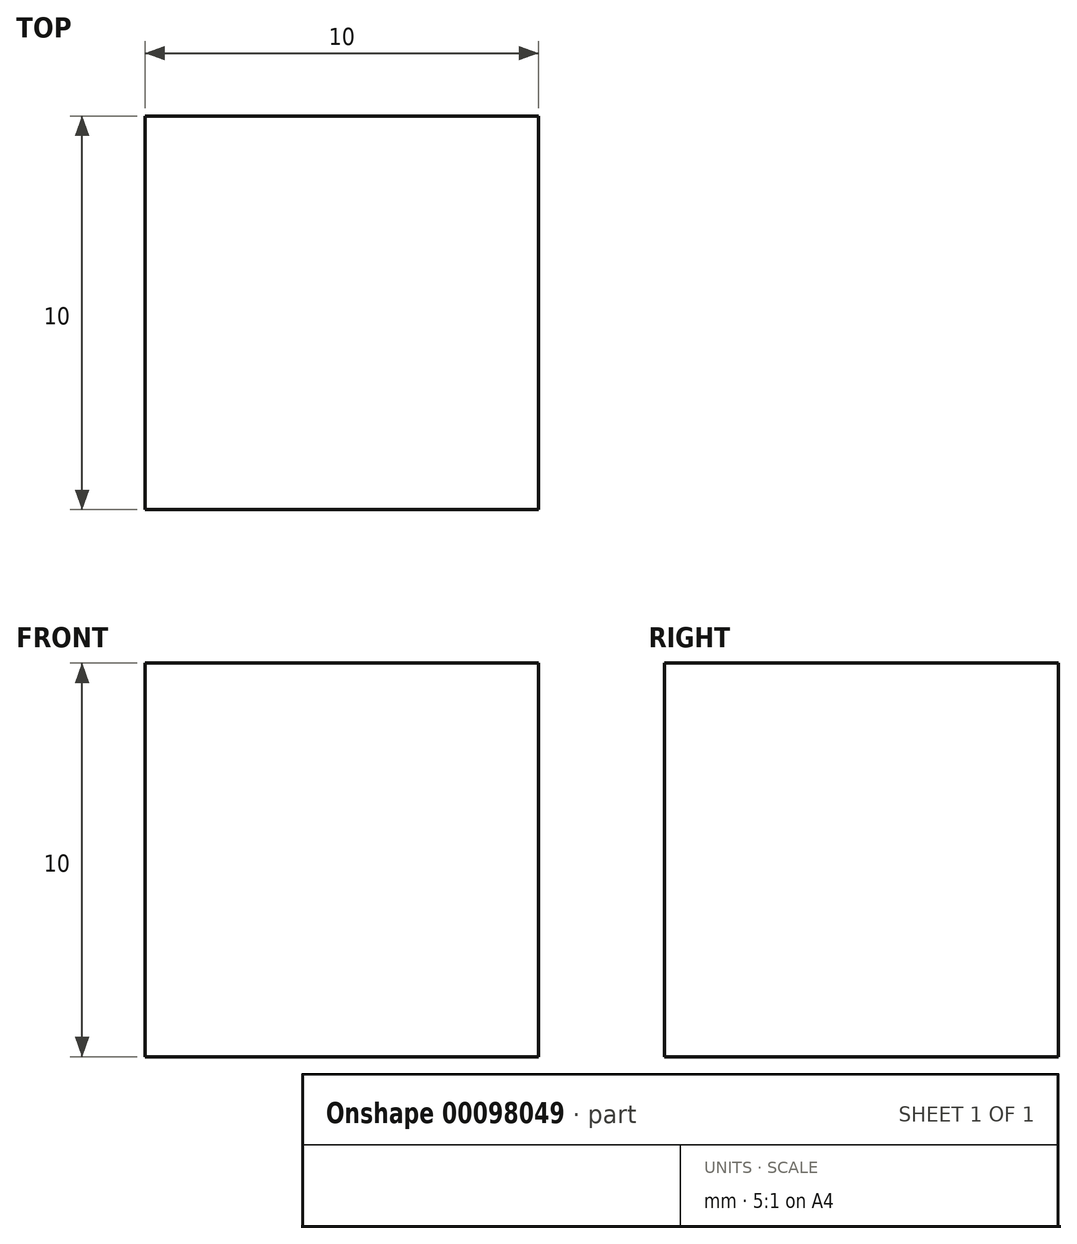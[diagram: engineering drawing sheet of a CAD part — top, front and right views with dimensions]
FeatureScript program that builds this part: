
annotation { "Feature Type Name" : "Feature", "Feature Type Description" : "" }
export const myFeature = defineFeature(function(context is Context, id is Id, definition is map)
    precondition{}
    {
        {
            var Q0;
            Q0=qCreatedBy(makeId("Top.planeOp"),FACE);
            var sketch = newSketch(context, id + "F0", { "sketchPlane" : qUnion([Q0])});
            skLineSegment(sketch, "E0.bottom", {"start": v(0, 0) * mm, "end": v(10, 0) * mm});
            skLineSegment(sketch, "E0.top", {"start": v(0, 10) * mm, "end": v(10, 10) * mm});
            skLineSegment(sketch, "E0.left", {"start": v(0, 0) * mm, "end": v(0, 10) * mm});
            skLineSegment(sketch, "E0.right", {"start": v(10, 0) * mm, "end": v(10, 10) * mm});
            skSolve(sketch);
        }
        {
            var Q0;
            Q0 = qSketchRegion(id + "F0", true);
            extrude(context, id + "F1", {"entities" : qUnion([Q0]), "depth" : 10 * mm});
        }
    });
